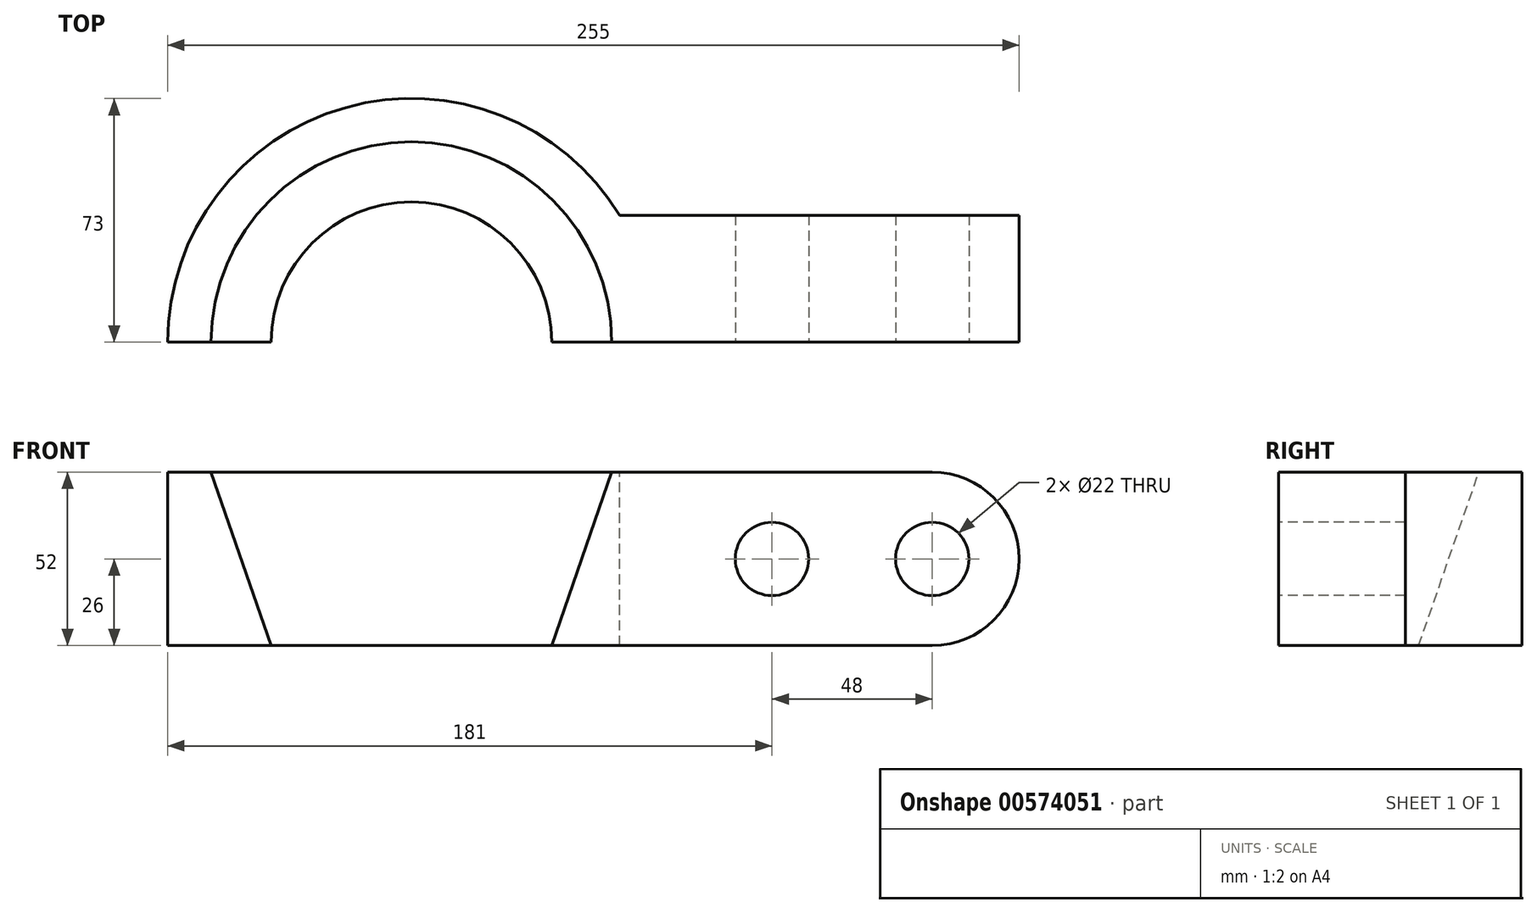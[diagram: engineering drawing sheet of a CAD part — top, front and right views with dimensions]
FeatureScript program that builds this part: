
annotation { "Feature Type Name" : "Feature", "Feature Type Description" : "" }
export const myFeature = defineFeature(function(context is Context, id is Id, definition is map)
    precondition{}
    {
        {
            var Q0;
            Q0=qCreatedBy(makeId("Front.planeOp"),FACE);
            var sketch = newSketch(context, id + "F0", { "sketchPlane" : qUnion([Q0])});
            skLineSegment(sketch, "E0", {"start": v(-73, 0) * mm, "end": v(-73, -52) * mm});
            skLineSegment(sketch, "E1", {"start": v(-73, -52) * mm, "end": v(-42, -52) * mm});
            skLineSegment(sketch, "E2", {"start": v(-42, -52) * mm, "end": v(-60, 0) * mm});
            skLineSegment(sketch, "E3", {"start": v(-60, 0) * mm, "end": v(-73, 0) * mm});
            skLineSegment(sketch, "E4", {"start": v(0, 69.83) * mm, "end": v(0, -82.04) * mm, "construction": true});
            skSolve(sketch);
        }
        {
            var Q0;
            Q0=makeQuery(id+"F0.imprint","IMPRINT",FACE,{"disambiguationData":[TD([[makeQuery(id+"F0.imprint","IMPRINT",EDGE,{"derivedFrom":sQuery(id+"F0.wireOp",EDGE,"E0")}),1.0]])]});
            var Q1;
            Q1=sQuery(id+"F0.wireOp",EDGE,"E4");
            revolve(context, id + "F1", {"entities" : qUnion([Q0]), "axis" : qUnion([Q1]), "revolveType" : RevolveType.ONE_DIRECTION, "angle" : 180 * degree});
        }
        {
            var Q0;
            Q0=qCreatedBy(makeId("Front.planeOp"),FACE);
            var sketch = newSketch(context, id + "F2", { "sketchPlane" : qUnion([Q0])});
            skLineSegment(sketch, "E5.0", {"start": v(60, 0) * mm, "end": v(73, 0) * mm});
            skLineSegment(sketch, "E6.0", {"start": v(73, -52) * mm, "end": v(42, -52) * mm});
            skLineSegment(sketch, "E7.bottom", {"start": v(60, 0) * mm, "end": v(156, 0) * mm});
            skLineSegment(sketch, "E7.top", {"start": v(60, -52) * mm, "end": v(156, -52) * mm});
            skLineSegment(sketch, "E7.left", {"start": v(60, 0) * mm, "end": v(60, -52) * mm});
            skLineSegment(sketch, "E7.right", {"start": v(182, -26) * mm, "end": v(182, -26) * mm});
            skPoint(sketch, "E8.visualSharp", {"position": v(182, 0) * mm});
            skArc(sketch, "E8.filletArc", {"start": v(182, -26) * mm, "mid": v(174.38, -7.62) * mm, "end": v(156, 0) * mm});
            skPoint(sketch, "E9.visualSharp", {"position": v(182, -52) * mm});
            skArc(sketch, "E9.filletArc", {"start": v(156, -52) * mm, "mid": v(174.38, -44.38) * mm, "end": v(182, -26) * mm});
            skCircle(sketch, "E10", {"center": v(156, -26) * mm, "radius": 11 * mm});
            skCircle(sketch, "E11.1.0.0", {"center": v(108, -26) * mm, "radius": 11 * mm});
            skLineSegment(sketch, "E11.direction1", {"start": v(156, -26) * mm, "end": v(108, -26) * mm, "construction": true});
            skSolve(sketch);
        }
        {
            var Q0;
            {var subQ1=sQuery(id+"F2.wireOp",EDGE,"E7.left");Q0=makeQuery(id+"F2.imprint","IMPRINT",FACE,{"disambiguationData":[TD([[makeQuery(id+"F2.imprint","IMPRINT",EDGE,{"derivedFrom":subQ1}),1.0]])]});}
            extrude(context, id + "F3", {"entities" : qUnion([Q0]), "operationType" : NewBodyOperationType.ADD, "oppositeDirection" : true, "depth" : 38 * mm, "offsetDistance" : 25 * mm});
        }
    });
